# Revit family: Quiet-RndTop_SqrBase
name_source: partatom
category: Furniture
revit_build: Autodesk Revit 2016 (Build: 20150714_1515(x64)
units: mm (PartAtom-declared; Revit-internal decimal feet)

## family parameters
Always vertical = Yes
Cut with Voids When Loaded = No
OmniClass Number = 23.40.20.14.14.17
OmniClass Title = Stools
Room Calculation Point = No
Shared = No
Work Plane-Based = No

## types (18) — shared parameters
Manufacturer = Bernhardt Design
URL = http://bernhardtdesign.com

## per-type parameters (varying)
| type | Base Width | Catalog | Column Radius | Depth | Height | SKU | Top Radius | Width |
| Quiet - QUS-182 18" rnd top/ sqr base occasional | 12" | QUS-182 | 3/8" | 18" | 18" | QUS-182 | 9" | 18" |
| Quiet - QUS-222 22" rnd top/ sqr base occasional | 16" | QUS-222 | 3/8" | 22" | 18" | QUS-222 | 11" | 22" |
| Quiet - QUS-302 30" rnd top/ sqr base occasional | 17 3/4" | QUS-302 | 1 1/2" | 30" | 13" | QUS-302 | 15" | 30" |
| Quiet - QUS-362 36" rnd top/ sqr base occasional | 17 3/4" | QUS-362 | 1 1/2" | 36" | 13" | QUS-362 | 18" | 36" |
| Quiet - QUS-422 42" rnd top/ sqr base occasional | 21 5/8" | QUS-422 | 1 1/2" | 42" | 13" | QUS-422 | 21" | 42" |
| Quiet - QUS-186 18" rnd top/ sqr base mid | 12" | QUS-186 | 7/16" | 18" | 23 3/4" | QUS-186 | 9" | 18" |
| Quiet - QUS-226 22" rnd top/ sqr base mid | 16" | QUS-226 | 7/16" | 22" | 23 3/4" | QUS-226 | 11" | 22" |
| Quiet - QUS-306 30" rnd top/ sqr base mid | 17 3/4" | QUS-306 | 1 1/2" | 30" | 23 3/4" | QUS-306 | 15" | 30" |
| Quiet - QUS-366 36" rnd top/ sqr base mid | 17 3/4" | QUS-366 | 1 1/2" | 36" | 23 3/4" | QUS-366 | 18" | 36" |
| Quiet - QUS-426 42" rnd top/ sqr base mid | 21 5/8" | QUS-426 | 1 1/2" | 42" | 23 3/4" | QUS-426 | 21" | 42" |
| Quiet - QUS-310 30" rnd top/ sqr base conference | 17 3/4" | QUS-310 | 1 1/2" | 30" | 29" | QUS-310 | 15" | 30" |
| Quiet - QUS-370 36" rnd top/ sqr base conference | 17 3/4" | QUS-370 | 1 1/2" | 36" | 29" | QUS-370 | 18" | 36" |
| Quiet - QUS-430 42" rnd top/ sqr base conference | 21 5/8" | QUS-430 | 1 1/2" | 42" | 29" | QUS-430 | 21" | 42" |
| Quiet - QUS-272 27" rnd top/ sqr base bar | 17 3/4" | QUS-272 | 1 1/2" | 27" | 42" | QUS-272 | 13 1/2" | 27" |
| Quiet - QUS-486 48" rnd top/ sqr base mid | 21 5/8" | QUS-486 | 1 1/2" | 48" | 23 3/4" | QUS-486 | 24" | 48" |
| Quiet - QUS-482 48" rnd top/ sqr base occasional | 21 5/8" | QUS-482 | 1 1/2" | 48" | 13" | QUS-482 | 24" | 48" |
| Quiet - QUS-488 48" rnd top/ sqr base conference | 21 5/8" | QUS-488 | 1 1/2" | 48" | 29" | QUS-488 | 24" | 48" |
| Quiet - QUS-314 30" rnd top/ sqr base bar | 17 3/4" | QUS-314 | 1 1/2" | 30" | 42" | QUS-314 | 15" | 30" |

## geometry (parser evidence)
native form markers: Blend x8, Sweep x2
no freeform markers — native parametric forms only
